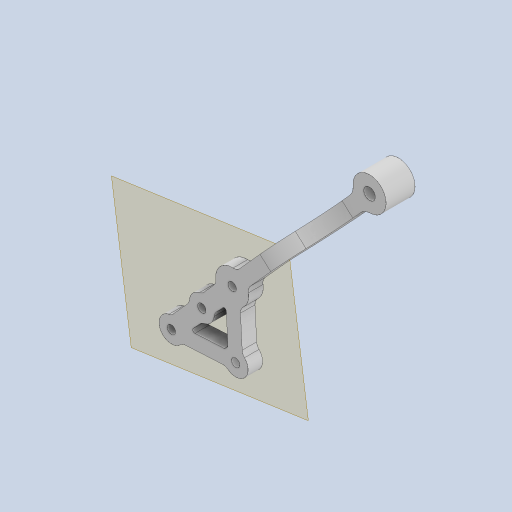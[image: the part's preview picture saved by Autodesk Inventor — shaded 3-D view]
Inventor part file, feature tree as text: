
AUTODESK INVENTOR PART (.ipt)
format: ipt  version: 2023 (Build 270158000, 158)  size: 358,912 bytes
history: native  units: mm
features: extrude x9, sketch x9, projected_geometry x9, other x5, fillet x4, thicken_offset x2, reference x2, plane x1
ambient origin geometry x8: Origin, YZ Plane, XZ Plane, XY Plane, X Axis, Y Axis, Z Axis, Center Point
bodies: Solid1 (feature_tree)
feature tree (41):
  extrude  "Extrusion1"  Depth=3.0mm
  plane  "Work Plane1"
  extrude  "Extrusion2"  Depth=7.0mm
  extrude  "Extrusion3"  Depth=2.0mm
  extrude  "Extrusion4"  Depth=6.0mm
  extrude  "Extrusion5"  Depth=4.0mm
  fillet  "Fillet1"  Radius=12.0mm
  fillet  "Fillet2"  Radius=3.5mm
  thicken_offset  "Thicken1"
  extrude  "Extrusion6"  Depth=3.5mm
  extrude  "Extrusion7"  Depth=5.0mm TaperAngle=0.0deg
  extrude  "Extrusion8"  Depth=4.0mm
  fillet  "Fillet4"  Radius=5.0mm
  extrude  "Extrusion9"  Depth=3.0mm
  fillet  "Fillet5"  Radius=2.0mm
  thicken_offset  "Thicken2"
  sketch  "Sketch1"  dims[d0=8.0mm d1=3.0mm]
  reference  "Reference1"
  sketch  "Sketch2"  dims[d2=7.0mm d3=0.0mm d4=11.0mm]
  reference  "Reference2"
  sketch  "Sketch3"  dims[d5=2.0mm d6=11.0mm]
  projected_geometry  "Projected Loop1"
  projected_geometry  "Projected Loop2"
  sketch  "Sketch4"  dims[d7=2.0mm d8=6.0mm]
  projected_geometry  "Projected Loop3"
  sketch  "Sketch5"  dims[d9=6.0mm d10=4.0mm d11=12.0mm d12=3.5mm]
  projected_geometry  "Projected Loop4"
  projected_geometry  "Projected Loop5"
  sketch  "Sketch6"  dims[d13=3.5mm d14=0.0mm d15=8.0mm]
  projected_geometry  "Projected Loop6"
  sketch  "Sketch7"  dims[d16=3.5mm d17=5.0mm d18=0.0mm]
  projected_geometry  "Projected Loop7"
  sketch  "Sketch8"  dims[d19=5.0mm d20=4.0mm d21=5.0mm d22=0.0mm]
  projected_geometry  "Projected Loop8"
  sketch  "Sketch9"  dims[d23=3.5mm d24=0.0mm d28=3.0mm d29=2.0mm d30=1.5mm d31=1.5mm d32=2.0mm d33=3.5mm d34=0.0mm d35=11.0mm d36=2.0mm d37=6.0mm d38=3.5mm d39=3.5mm d40=3.5mm d41=0.0mm d42=6.0mm d43=3.5mm d44=0.0mm d46=0.5mm d47=8.0mm d48=10.0mm d49=0.0mm d50=2.0mm d51=0.1mm d52=0.05mm]
  projected_geometry  "Projected Loop9"
  parser-record x1  (decoder bookkeeping rows leaked as tree rows — omitted from the tree; the rows remain in map.json)
  other  "leg_1.iam"
  other  "leg_link_1:1"
  other  "reducer_1:2"
  other  "tendon_wh_2:1"
note: 1 file-system path scrubbed to <path> (originals preserved in map.json)
